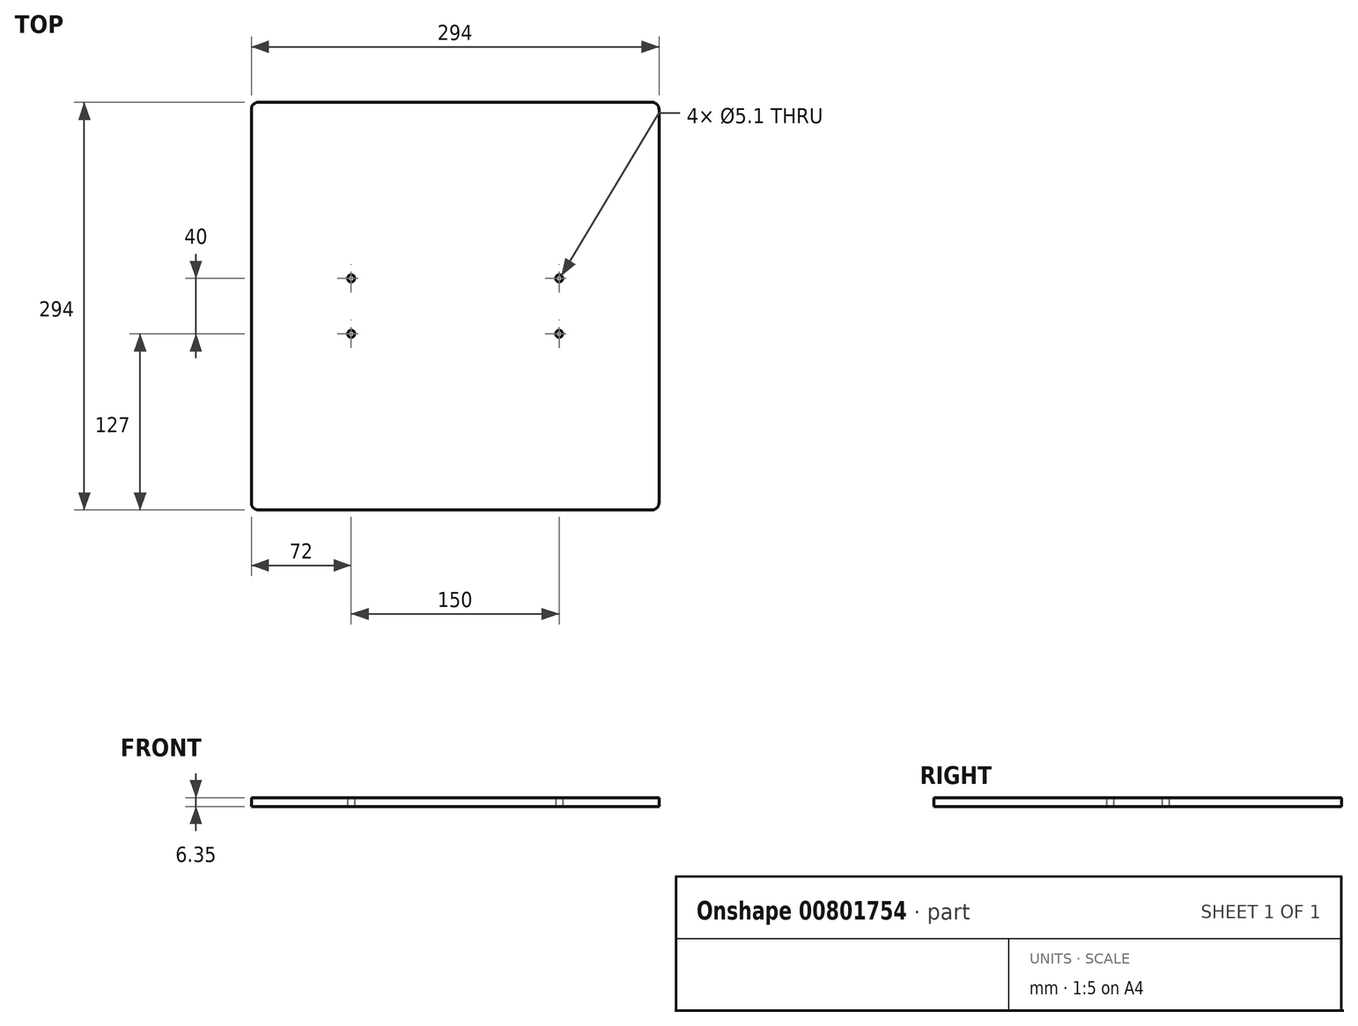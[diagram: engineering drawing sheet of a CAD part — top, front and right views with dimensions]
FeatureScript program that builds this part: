
annotation { "Feature Type Name" : "Feature", "Feature Type Description" : "" }
export const myFeature = defineFeature(function(context is Context, id is Id, definition is map)
    precondition{}
    {
        {
            var Q0;
            Q0=qCreatedBy(makeId("Top.planeOp"),FACE);
            var sketch = newSketch(context, id + "F0", { "sketchPlane" : qUnion([Q0])});
            skLineSegment(sketch, "E0.bottom", {"start": v(142, 147) * mm, "end": v(-142, 147) * mm});
            skLineSegment(sketch, "E0.top", {"start": v(142, -147) * mm, "end": v(-142, -147) * mm});
            skLineSegment(sketch, "E0.left", {"start": v(147, 142) * mm, "end": v(147, -142) * mm});
            skLineSegment(sketch, "E0.right", {"start": v(-147, 142) * mm, "end": v(-147, -142) * mm});
            skPoint(sketch, "E0.middle", {"position": v(0, 0) * mm});
            skLineSegment(sketch, "E1.bottom", {"start": v(75, 20) * mm, "end": v(-75, 20) * mm, "construction": true});
            skLineSegment(sketch, "E1.top", {"start": v(75, -20) * mm, "end": v(-75, -20) * mm, "construction": true});
            skLineSegment(sketch, "E1.left", {"start": v(75, 20) * mm, "end": v(75, -20) * mm, "construction": true});
            skLineSegment(sketch, "E1.right", {"start": v(-75, 20) * mm, "end": v(-75, -20) * mm, "construction": true});
            skCircle(sketch, "E2", {"center": v(75, 20) * mm, "radius": 2.55 * mm});
            skCircle(sketch, "E3", {"center": v(75, -20) * mm, "radius": 2.55 * mm});
            skCircle(sketch, "E4", {"center": v(-75, -20) * mm, "radius": 2.55 * mm});
            skCircle(sketch, "E5", {"center": v(-75, 20) * mm, "radius": 2.55 * mm});
            skPoint(sketch, "E6.visualSharp", {"position": v(147, 147) * mm});
            skArc(sketch, "E6.filletArc", {"start": v(147, 142) * mm, "mid": v(145.54, 145.54) * mm, "end": v(142, 147) * mm});
            skPoint(sketch, "E7.visualSharp", {"position": v(147, -147) * mm});
            skArc(sketch, "E7.filletArc", {"start": v(142, -147) * mm, "mid": v(145.54, -145.54) * mm, "end": v(147, -142) * mm});
            skPoint(sketch, "E8.visualSharp", {"position": v(-147, -147) * mm});
            skArc(sketch, "E8.filletArc", {"start": v(-147, -142) * mm, "mid": v(-145.54, -145.54) * mm, "end": v(-142, -147) * mm});
            skPoint(sketch, "E9.visualSharp", {"position": v(-147, 147) * mm});
            skArc(sketch, "E9.filletArc", {"start": v(-142, 147) * mm, "mid": v(-145.54, 145.54) * mm, "end": v(-147, 142) * mm});
            skSolve(sketch);
        }
        {
            var Q0;
            Q0=makeQuery(id+"F0.imprint","IMPRINT",FACE,{"disambiguationData":[TD([[makeQuery(id+"F0.imprint","IMPRINT",EDGE,{"derivedFrom":sQuery(id+"F0.wireOp",EDGE,"E0.bottom")}),1.0]])]});
            extrude(context, id + "F1", {"entities" : qUnion([Q0]), "depth" : 6.35 * mm, "offsetDistance" : 25 * mm});
        }
    });
